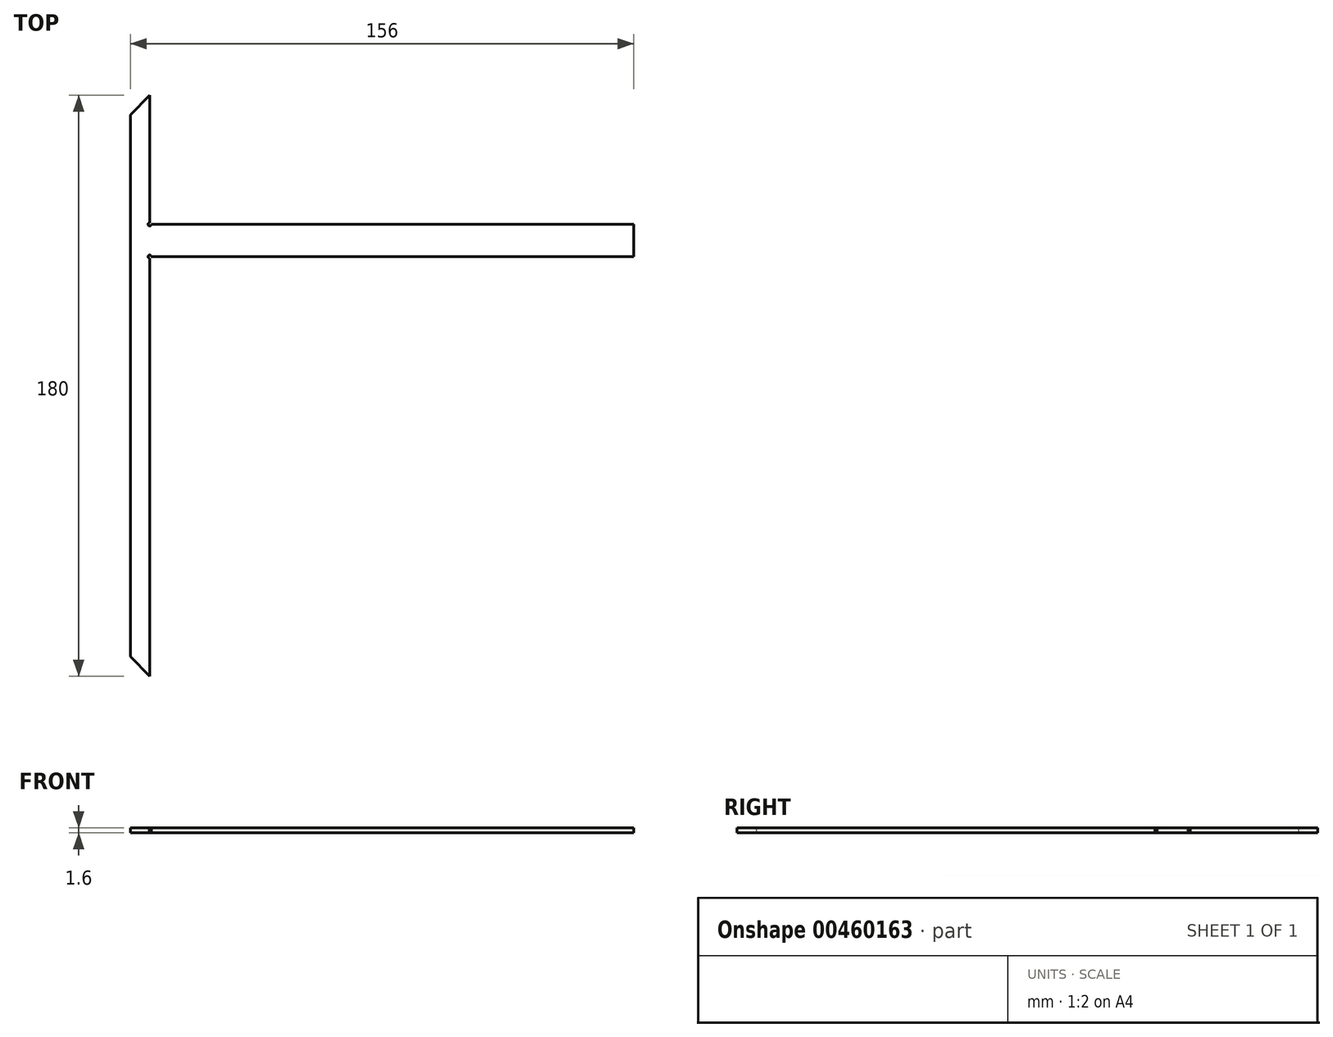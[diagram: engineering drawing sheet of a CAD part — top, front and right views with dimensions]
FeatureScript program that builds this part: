
annotation { "Feature Type Name" : "Feature", "Feature Type Description" : "" }
export const myFeature = defineFeature(function(context is Context, id is Id, definition is map)
    precondition{}
    {
        {
            var Q0;
            Q0=qCreatedBy(makeId("Top.planeOp"),FACE);
            var sketch = newSketch(context, id + "F0", { "sketchPlane" : qUnion([Q0])});
            skLineSegment(sketch, "E0", {"start": v(0.5, 0) * mm, "end": v(150, 0) * mm});
            skLineSegment(sketch, "E1", {"start": v(150, 0) * mm, "end": v(150, -10) * mm});
            skLineSegment(sketch, "E2", {"start": v(150, -10) * mm, "end": v(0.5, -10) * mm});
            skLineSegment(sketch, "E3", {"start": v(0, -10.5) * mm, "end": v(0, -140) * mm});
            skLineSegment(sketch, "E4", {"start": v(0, -140) * mm, "end": v(-6, -134) * mm});
            skLineSegment(sketch, "E5", {"start": v(-6, -134) * mm, "end": v(-6, 34) * mm});
            skLineSegment(sketch, "E6", {"start": v(-6, 34) * mm, "end": v(0, 40) * mm});
            skLineSegment(sketch, "E7", {"start": v(0, 40) * mm, "end": v(0, 0.5) * mm});
            skArc(sketch, "E8", {"start": v(0, 0.5) * mm, "mid": v(-0.35, -0.35) * mm, "end": v(0.5, 0) * mm});
            skArc(sketch, "E9", {"start": v(0.5, -10) * mm, "mid": v(-0.35, -9.65) * mm, "end": v(0, -10.5) * mm});
            skSolve(sketch);
        }
        {
            var Q0;
            Q0 = qSketchRegion(id + "F0", true);
            extrude(context, id + "F1", {"entities" : qUnion([Q0]), "depth" : 1.6 * mm});
        }
    });
